# Revit family: IS_Iom_A9125_BIM_NL
name_source: partatom
category: Plumbing Fixtures
revit_build: Autodesk Revit MEP 2016 (Build: 20161004_0715(x64)
units: mm (PartAtom-declared; Revit-internal decimal feet)

## family parameters
Always vertical = No
Cut with Voids When Loaded = No
OmniClass Number = 23.45.05.14.21.11
OmniClass Title = Bath/Shower Units
Part Type = Normal
Room Calculation Point = No
Round Connector Dimension = Use Diameter
Shared = No
Work Plane-Based = No

## types (1)
- A9125AA IOM LEGPLANK IN TRANSPARANT GLAS 520 MM
    Accesoires = www.idealstandardnederland.nl
    Afmetingen = 0
    Afwerking = Chroom
    Artikelnummer = A9125AA
    Artikelomschrijving = ISI_IOM_Shelves_A9125AA
    Artikelreferentie = IOM LEGPLANK IN TRANSPARANT GLAS 520 MM
    Auteur = Ideal Standard
    BIMobject category = Storage
    BOSUseNativeGeometries = 1
    Barcode = 4015413327992
    Beschrijvinggarantie = 4015413327992
    Brand url = www.idealstandardnederland.nl
    Breedte = 250
    BrutoGewicht = 0
    Cost = 0 $
    Description = IOM LEGPLANK IN TRANSPARANT GLAS 520 MM
    Diepte = 360 mm  [stored 1.1811 ft]
    EAN code = https://4015413327992
    Edition number = 1
    Eigenschappen = Glazen legplank 520 mm. Inclusief bevestigingsset. Legplank van transparant glas. Houder van metaal. 4 geïntegreerde bevestigingspunten.
    Garantieonderdelen = 1
    Garantieunits = Jaar
    Hoogte = 120
    IFC Classification = Sanitary Terminal
    IfcExportAs = Ifc Sanitary Terminal Type
    Installatieinstructies = http://www.idealstandardnederland.nl
    Installation instructions = www.idealstandardnederland.nl
    Kleur = Chroom
    Lengte = 360 mm  [stored 1.1811 ft]
    Manufacturer = www.idealstandardnederland.nl
    Manufacturer name = Ideal Standard
    Materiaal = Glas
    Merk = Ideal Standard
    Model = A9125AA
    NBS Reference Code = 35-77-80
    NBS Reference Description = Shelves
    Nettogewicht = 0
    Nominal height = 48
    Nominal width = 520
    NominalHeight = 48 mm  [stored 0.15748 ft]
    NominalLength = 138 mm
    NominalWidth = 520 mm  [stored 1.70604 ft]
    OmniClass Code = 23-21 11 11 11
    OmniClass Description = Commercial Storage Shelves
    Product Guid = b1c8ce94-bbe0-42f8-9328-75bc5fcf4adb
    Product SKU = A9125
    Product data url = https://bimobject.com
    Product family = IOM
    Product group = Shelf
    Product name = IOM glass shelf 520x138mm
    QR code = http://bimobject.com
    Revisie = 1
    Size = 520x138x48 mm
    Technical description = www.idealstandardnederland.nl
    Telefoonnummer = 31 (0) 77 355 08 08
    Typeconnectie = Sanitair
    URL = www.idealstandardnederland.nl
    Uniclass 1.4 Code = L8261
    Uniclass 1.4 Description = Shelves
    Uniclass 2.0 Code = PR-35-77-80
    Uniclass 2.0 Description = Shelves
    Uniclass 2015 Code = Pr_40_30_78_78
    Uniclass 2015 Name = Shelves
    Uniclass2015Beschrijving = Bathroom shelves
    Uniclass2015Referentie = Pr_40_30_78_06
    Uniclass2015Version = Products v1.1
    Versie = 1
    Vervangingskosten = 0
    Volumeunits = Liter
    Weight Net (Kg) = 1.45

note: [stored X ft] marks values corroborated as IEEE doubles in the binary element streams (Revit-internal decimal feet)

## geometry (parser evidence)
native form markers: Blend x2, Sweep x3
no freeform markers — native parametric forms only
